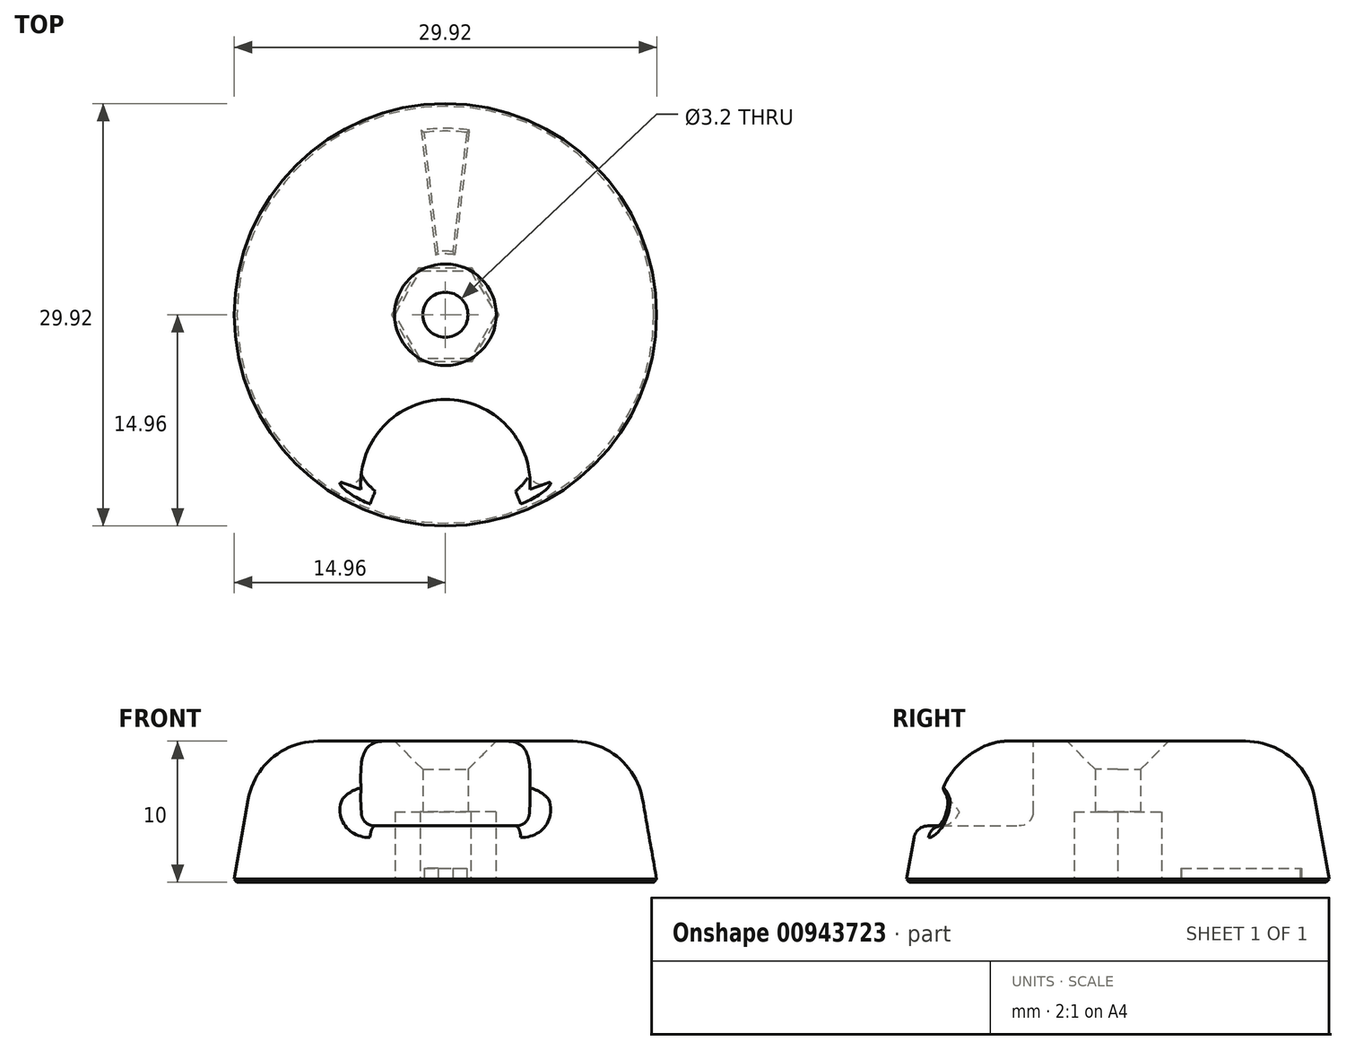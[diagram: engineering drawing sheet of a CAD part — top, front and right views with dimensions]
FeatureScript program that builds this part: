
annotation { "Feature Type Name" : "Feature", "Feature Type Description" : "" }
export const myFeature = defineFeature(function(context is Context, id is Id, definition is map)
    precondition{}
    {
        {
            var Q0;
            Q0=qCreatedBy(makeId("Top.planeOp"),FACE);
            var sketch = newSketch(context, id + "F0", { "sketchPlane" : qUnion([Q0])});
            skCircle(sketch, "E0", {"center": v(0, 0) * mm, "radius": 15 * mm});
            skSolve(sketch);
        }
        {
            var Q0;
            Q0 = qSketchRegion(id + "F0", true);
            extrude(context, id + "F1", {"entities" : qUnion([Q0]), "depth" : 10 * mm, "offsetDistance" : 25 * mm, "hasDraft" : true, "draftAngle" : 10 * degree, "draftPullDirection" : true});
        }
        {
            var Q0;
            Q0=makeQuery(id+"F1.opExtrude","CAP_EDGE",EDGE,{"disambiguationData":[OSD([sQuery(id+"F0.wireOp",EDGE,"E0")])],"isStart":false});
            fillet(context, id + "F2", {"entities" : qUnion([Q0]), "radius" : 5 * mm, "tangentPropagation" : true, "allowEdgeOverflow" : false});
        }
        {
            var Q0;
            Q0=makeQuery(id+"F1.opExtrude","CAP_FACE",FACE,{"disambiguationData":[OSD([sQuery(id+"F0.wireOp",EDGE,"E0")])],"isStart":false});
            var sketch = newSketch(context, id + "F3", { "sketchPlane" : qUnion([Q0])});
            skCircle(sketch, "E1", {"center": v(0, -12) * mm, "radius": 6 * mm});
            skSolve(sketch);
        }
        {
            var Q0;
            Q0 = qSketchRegion(id + "F3", true);
            extrude(context, id + "F4", {"entities" : qUnion([Q0]), "operationType" : NewBodyOperationType.REMOVE, "oppositeDirection" : true, "depth" : 6 * mm, "offsetDistance" : 25 * mm});
        }
        {
            var Q0;
            Q0=makeQuery(id+"F4.boolean.opBoolean","COPY",EDGE,{"derivedFrom":makeQuery(id+"F4.opExtrude","CAP_EDGE",EDGE,{"disambiguationData":[OSD([sQuery(id+"F3.wireOp",EDGE,"E1")])],"isStart":true})});
            var Q1;
            Q1=makeQuery(id+"Fh2hTOuDvYVRQE6_1.1.F4.boolean.opBoolean","COPY",EDGE,{"derivedFrom":makeQuery(id+"Fh2hTOuDvYVRQE6_1.1.F4.opExtrude","CAP_EDGE",EDGE,{"disambiguationData":[OSD([sQuery(id+"F3.wireOp",EDGE,"E1")])],"isStart":true})});
            var Q2;
            Q2=makeQuery(id+"Fh2hTOuDvYVRQE6_1.2.F4.boolean.opBoolean","COPY",EDGE,{"derivedFrom":makeQuery(id+"Fh2hTOuDvYVRQE6_1.2.F4.opExtrude","CAP_EDGE",EDGE,{"disambiguationData":[OSD([sQuery(id+"F3.wireOp",EDGE,"E1")])],"isStart":true})});
            var Q3;
            Q3=makeQuery(id+"Fh2hTOuDvYVRQE6_1.3.F4.boolean.opBoolean","COPY",EDGE,{"derivedFrom":makeQuery(id+"Fh2hTOuDvYVRQE6_1.3.F4.opExtrude","CAP_EDGE",EDGE,{"disambiguationData":[OSD([sQuery(id+"F3.wireOp",EDGE,"E1")])],"isStart":true})});
            var Q4;
            Q4=makeQuery(id+"Fh2hTOuDvYVRQE6_1.4.F4.boolean.opBoolean","COPY",EDGE,{"derivedFrom":makeQuery(id+"Fh2hTOuDvYVRQE6_1.4.F4.opExtrude","CAP_EDGE",EDGE,{"disambiguationData":[OSD([sQuery(id+"F3.wireOp",EDGE,"E1")])],"isStart":true})});
            var Q5;
            Q5=makeQuery(id+"Fh2hTOuDvYVRQE6_1.5.F4.boolean.opBoolean","COPY",EDGE,{"derivedFrom":makeQuery(id+"Fh2hTOuDvYVRQE6_1.5.F4.opExtrude","CAP_EDGE",EDGE,{"disambiguationData":[OSD([sQuery(id+"F3.wireOp",EDGE,"E1")])],"isStart":true})});
            var Q6;
            Q6=makeQuery(id+"Fh2hTOuDvYVRQE6_1.5.F4.boolean.opBoolean","COPY",FACE,{"derivedFrom":makeQuery(id+"Fh2hTOuDvYVRQE6_1.5.F4.opExtrude","CAP_FACE",FACE,{"disambiguationData":[OSD([sQuery(id+"F3.wireOp",EDGE,"E1")])],"isStart":false})});
            var Q7;
            Q7=makeQuery(id+"F4.boolean.opBoolean","COPY",FACE,{"derivedFrom":makeQuery(id+"F4.opExtrude","CAP_FACE",FACE,{"disambiguationData":[OSD([sQuery(id+"F3.wireOp",EDGE,"E1")])],"isStart":false})});
            var Q8;
            Q8=makeQuery(id+"Fh2hTOuDvYVRQE6_1.1.F4.boolean.opBoolean","COPY",FACE,{"derivedFrom":makeQuery(id+"Fh2hTOuDvYVRQE6_1.1.F4.opExtrude","CAP_FACE",FACE,{"disambiguationData":[OSD([sQuery(id+"F3.wireOp",EDGE,"E1")])],"isStart":false})});
            var Q9;
            Q9=makeQuery(id+"Fh2hTOuDvYVRQE6_1.2.F4.boolean.opBoolean","COPY",FACE,{"derivedFrom":makeQuery(id+"Fh2hTOuDvYVRQE6_1.2.F4.opExtrude","CAP_FACE",FACE,{"disambiguationData":[OSD([sQuery(id+"F3.wireOp",EDGE,"E1")])],"isStart":false})});
            var Q10;
            Q10=makeQuery(id+"Fh2hTOuDvYVRQE6_1.3.F4.boolean.opBoolean","COPY",FACE,{"derivedFrom":makeQuery(id+"Fh2hTOuDvYVRQE6_1.3.F4.opExtrude","CAP_FACE",FACE,{"disambiguationData":[OSD([sQuery(id+"F3.wireOp",EDGE,"E1")])],"isStart":false})});
            var Q11;
            Q11=makeQuery(id+"Fh2hTOuDvYVRQE6_1.4.F4.boolean.opBoolean","COPY",FACE,{"derivedFrom":makeQuery(id+"Fh2hTOuDvYVRQE6_1.4.F4.opExtrude","CAP_FACE",FACE,{"disambiguationData":[OSD([sQuery(id+"F3.wireOp",EDGE,"E1")])],"isStart":false})});
            fillet(context, id + "F5", {"entities" : qUnion([Q0, Q1, Q2, Q3, Q4, Q5, Q6, Q7, Q8, Q9, Q10, Q11]), "radius" : 1 * mm, "tangentPropagation" : true, "allowEdgeOverflow" : false});
        }
        {
            var Q0;
            Q0=makeQuery(id+"F1.opExtrude","CAP_FACE",FACE,{"disambiguationData":[OSD([sQuery(id+"F0.wireOp",EDGE,"E0")])],"isStart":true});
            var sketch = newSketch(context, id + "F6", { "sketchPlane" : qUnion([Q0])});
            skCircle(sketch, "E2.cCircle", {"center": v(0, 0) * mm, "radius": 3.1 * mm, "construction": true});
            skLineSegment(sketch, "E2.0", {"start": v(1.79, -3.1) * mm, "end": v(-1.79, -3.1) * mm});
            skLineSegment(sketch, "E2.1", {"start": v(-1.79, -3.1) * mm, "end": v(-3.58, 0) * mm});
            skLineSegment(sketch, "E2.2", {"start": v(-3.58, 0) * mm, "end": v(-1.79, 3.1) * mm});
            skLineSegment(sketch, "E2.3", {"start": v(-1.79, 3.1) * mm, "end": v(1.79, 3.1) * mm});
            skLineSegment(sketch, "E2.4", {"start": v(1.79, 3.1) * mm, "end": v(3.58, 0) * mm});
            skLineSegment(sketch, "E2.5", {"start": v(3.58, 0) * mm, "end": v(1.79, -3.1) * mm});
            skPoint(sketch, "E2.0.midPoint", {"position": v(0, -3.1) * mm});
            skSolve(sketch);
        }
        {
            var Q0;
            Q0 = qSketchRegion(id + "F6", true);
            extrude(context, id + "F7", {"entities" : qUnion([Q0]), "operationType" : NewBodyOperationType.REMOVE, "oppositeDirection" : true, "depth" : 5 * mm, "offsetDistance" : 25 * mm});
        }
        {
            var Q0;
            Q0=makeQuery(id+"F7.boolean.opBoolean","COPY",FACE,{"derivedFrom":makeQuery(id+"F7.opExtrude","CAP_FACE",FACE,{"disambiguationData":[OSD([sQuery(id+"F6.wireOp",EDGE,"E2.0"),sQuery(id+"F6.wireOp",EDGE,"E2.1"),sQuery(id+"F6.wireOp",EDGE,"E2.2"),sQuery(id+"F6.wireOp",EDGE,"E2.3"),sQuery(id+"F6.wireOp",EDGE,"E2.4"),sQuery(id+"F6.wireOp",EDGE,"E2.5")])],"isStart":false})});
            var sketch = newSketch(context, id + "F8", { "sketchPlane" : qUnion([Q0])});
            skCircle(sketch, "E3", {"center": v(0, 0) * mm, "radius": 1.6 * mm});
            skSolve(sketch);
        }
        {
            var Q0;
            Q0 = qSketchRegion(id + "F8", true);
            extrude(context, id + "F9", {"entities" : qUnion([Q0]), "operationType" : NewBodyOperationType.REMOVE, "oppositeDirection" : true, "depth" : 25 * mm, "offsetDistance" : 25 * mm});
        }
        {
            var Q0;
            Q0=makeQuery(id+"F9.boolean.opBoolean","INTERSECT",EDGE,{"derivedFrom":[makeQuery(id+"F1.opExtrude","CAP_FACE",FACE,{"disambiguationData":[OSD([sQuery(id+"F0.wireOp",EDGE,"E0")])],"isStart":false}),makeQuery(id+"F9.opExtrude","SWEPT_FACE",FACE,{"disambiguationData":[OSD([sQuery(id+"F8.wireOp",EDGE,"E3")])]})]});
            chamfer(context, id + "F10", {"entities" : qUnion([Q0]), "width" : 2 * mm, "tangentPropagation" : true});
        }
        {
            var Q0;
            Q0=makeQuery(id+"F1.opExtrude","CAP_FACE",FACE,{"disambiguationData":[OSD([sQuery(id+"F0.wireOp",EDGE,"E0")])],"isStart":true});
            var sketch = newSketch(context, id + "F11", { "sketchPlane" : qUnion([Q0])});
            skLineSegment(sketch, "E4", {"start": v(-0.52, -4.47) * mm, "end": v(-1.5, -12.91) * mm});
            skLineSegment(sketch, "E5", {"start": v(0.52, -4.47) * mm, "end": v(1.5, -12.91) * mm});
            skArc(sketch, "E6", {"start": v(-0.52, -4.47) * mm, "mid": v(0, -4.5) * mm, "end": v(0.52, -4.47) * mm});
            skArc(sketch, "E7", {"start": v(-1.5, -12.91) * mm, "mid": v(0, -13) * mm, "end": v(1.5, -12.91) * mm});
            skPoint(sketch, "E8.orphan", {"position": v(1.73, -14.9) * mm});
            skPoint(sketch, "E9.orphan", {"position": v(-1.73, -14.9) * mm});
            skLineSegment(sketch, "E10", {"start": v(-1.5, -12.91) * mm, "end": v(1.5, -12.91) * mm, "construction": true});
            skLineSegment(sketch, "E11", {"start": v(0, -12.91) * mm, "end": v(0, 0) * mm, "construction": true});
            skSolve(sketch);
        }
        {
            var Q0;
            Q0 = qSketchRegion(id + "F11", true);
            extrude(context, id + "F12", {"entities" : qUnion([Q0]), "operationType" : NewBodyOperationType.REMOVE, "oppositeDirection" : true, "depth" : 1 * mm, "offsetDistance" : 25 * mm});
        }
        {
            var Q0;
            Q0=makeQuery(id+"F1.opExtrude","CAP_FACE",FACE,{"disambiguationData":[OSD([sQuery(id+"F0.wireOp",EDGE,"E0")])],"isStart":true});
            chamfer(context, id + "F13", {"entities" : qUnion([Q0]), "width" : 0.2 * mm, "tangentPropagation" : true});
        }
    });
